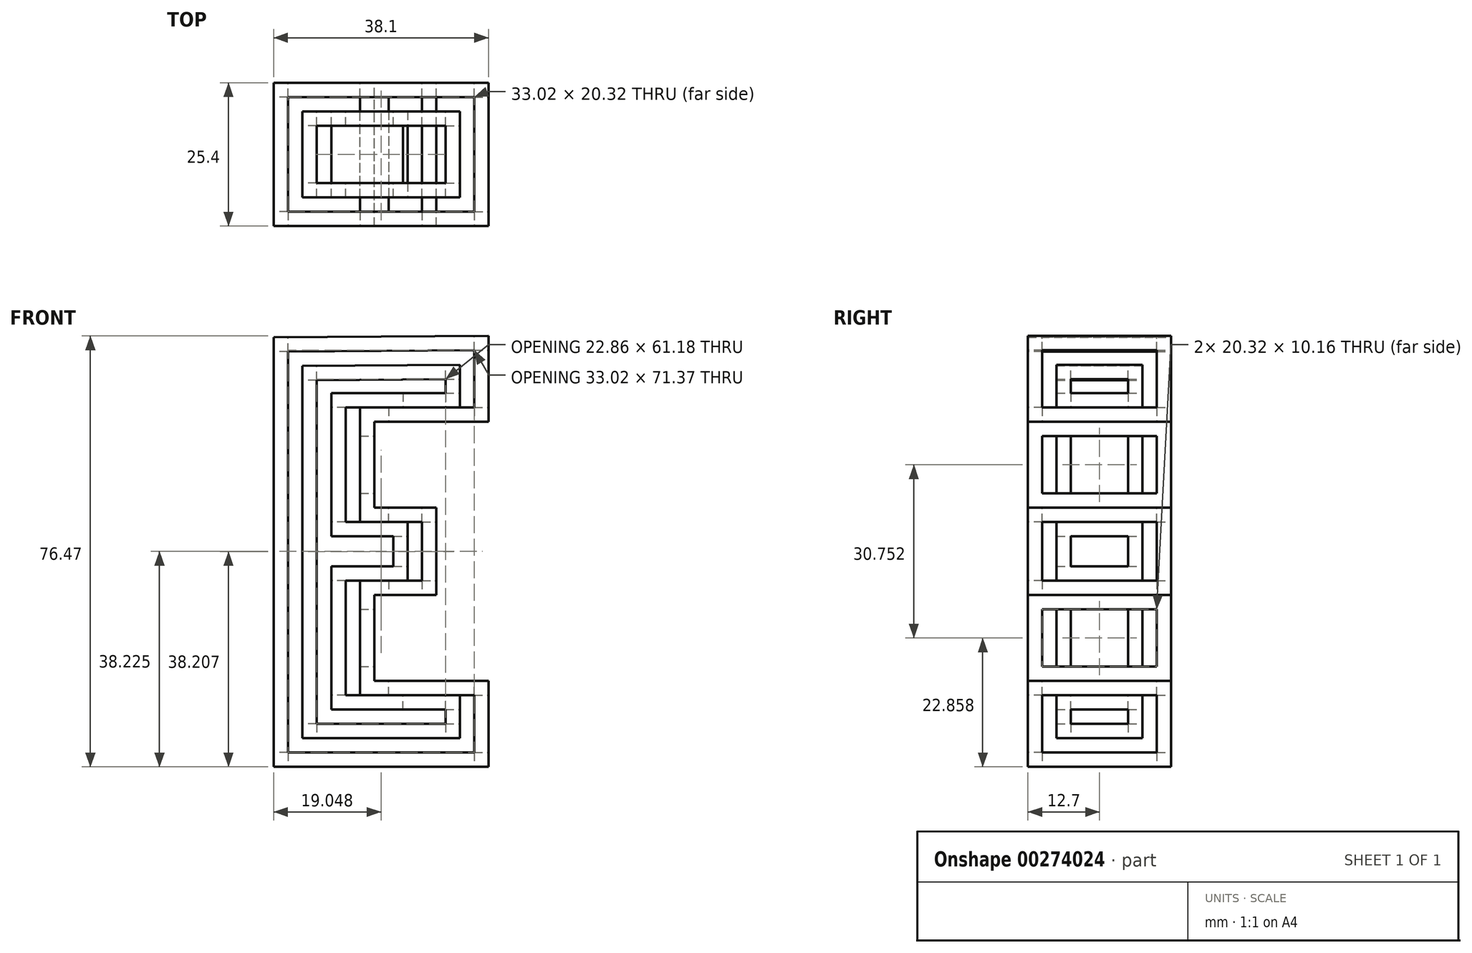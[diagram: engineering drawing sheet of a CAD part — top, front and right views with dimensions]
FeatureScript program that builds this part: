
annotation { "Feature Type Name" : "Feature", "Feature Type Description" : "" }
export const myFeature = defineFeature(function(context is Context, id is Id, definition is map)
    precondition{}
    {
        {
            var Q0;
            Q0=qCreatedBy(makeId("Front.planeOp"),FACE);
            var sketch = newSketch(context, id + "F0", { "sketchPlane" : qUnion([Q0])});
            skLineSegment(sketch, "E0", {"start": v(-49.34, 30.2) * mm, "end": v(-49.34, -46) * mm});
            skLineSegment(sketch, "E1", {"start": v(-11.24, -46) * mm, "end": v(-49.34, -46) * mm});
            skLineSegment(sketch, "E2", {"start": v(-11.24, -30.75) * mm, "end": v(-11.24, -46) * mm});
            skLineSegment(sketch, "E3", {"start": v(-31.48, -30.75) * mm, "end": v(-11.24, -30.75) * mm});
            skLineSegment(sketch, "E4", {"start": v(-31.48, -15.51) * mm, "end": v(-31.48, -30.75) * mm});
            skLineSegment(sketch, "E5", {"start": v(-20.49, -15.51) * mm, "end": v(-31.48, -15.51) * mm});
            skLineSegment(sketch, "E6", {"start": v(-20.49, 0) * mm, "end": v(-20.49, -15.51) * mm});
            skLineSegment(sketch, "E7", {"start": v(-31.48, 0) * mm, "end": v(-20.49, 0) * mm});
            skLineSegment(sketch, "E8", {"start": v(-31.48, 15.24) * mm, "end": v(-31.48, 0) * mm});
            skLineSegment(sketch, "E9", {"start": v(-31.48, 15.24) * mm, "end": v(-11.24, 15.24) * mm});
            skLineSegment(sketch, "E10", {"start": v(-11.24, 15.24) * mm, "end": v(-11.24, 30.48) * mm});
            skLineSegment(sketch, "E11", {"start": v(-11.24, 30.48) * mm, "end": v(-49.34, 30.2) * mm});
            skSolve(sketch);
        }
        {
            var Q0;
            Q0=makeQuery(id+"F0.imprint","IMPRINT",FACE,{"disambiguationData":[TD([[makeQuery(id+"F0.imprint","IMPRINT",EDGE,{"derivedFrom":sQuery(id+"F0.wireOp",EDGE,"E0")}),1.0]])]});
            extrude(context, id + "F1", {"entities" : qUnion([Q0]), "depth" : 12.7 * mm});
        }
        {
            var Q0;
            Q0=makeQuery(id+"F1.opExtrude","CAP_FACE",FACE,{"disambiguationData":[OSD([sQuery(id+"F0.wireOp",EDGE,"E0"),sQuery(id+"F0.wireOp",EDGE,"E1"),sQuery(id+"F0.wireOp",EDGE,"E2"),sQuery(id+"F0.wireOp",EDGE,"E3"),sQuery(id+"F0.wireOp",EDGE,"E4"),sQuery(id+"F0.wireOp",EDGE,"E5"),sQuery(id+"F0.wireOp",EDGE,"E6"),sQuery(id+"F0.wireOp",EDGE,"E7"),sQuery(id+"F0.wireOp",EDGE,"E8"),sQuery(id+"F0.wireOp",EDGE,"E9"),sQuery(id+"F0.wireOp",EDGE,"E10"),sQuery(id+"F0.wireOp",EDGE,"E11")])],"isStart":false});
            var sketch = newSketch(context, id + "F2", { "sketchPlane" : qUnion([Q0])});
            skLineSegment(sketch, "E12.0", {"start": v(-34.02, 17.78) * mm, "end": v(-13.78, 17.78) * mm});
            skLineSegment(sketch, "E12.1", {"start": v(-13.78, -43.45) * mm, "end": v(-13.78, -33.3) * mm});
            skLineSegment(sketch, "E12.2", {"start": v(-46.8, -43.45) * mm, "end": v(-13.78, -43.45) * mm});
            skLineSegment(sketch, "E12.3", {"start": v(-46.8, 27.69) * mm, "end": v(-46.8, -43.45) * mm});
            skLineSegment(sketch, "E12.4", {"start": v(-13.78, 27.92) * mm, "end": v(-46.8, 27.69) * mm});
            skLineSegment(sketch, "E12.5", {"start": v(-13.78, -33.3) * mm, "end": v(-34.02, -33.3) * mm});
            skLineSegment(sketch, "E12.6", {"start": v(-13.78, 17.78) * mm, "end": v(-13.78, 27.92) * mm});
            skLineSegment(sketch, "E12.7", {"start": v(-34.02, -33.3) * mm, "end": v(-34.02, -12.97) * mm});
            skLineSegment(sketch, "E12.8", {"start": v(-34.02, -12.97) * mm, "end": v(-23.03, -12.97) * mm});
            skLineSegment(sketch, "E12.9", {"start": v(-23.03, -12.97) * mm, "end": v(-23.03, -2.54) * mm});
            skLineSegment(sketch, "E12.10", {"start": v(-23.03, -2.54) * mm, "end": v(-34.02, -2.54) * mm});
            skLineSegment(sketch, "E12.11", {"start": v(-34.02, -2.54) * mm, "end": v(-34.02, 17.78) * mm});
            skSolve(sketch);
        }
        {
            var Q0;
            Q0=makeQuery(id+"F2.imprint","IMPRINT",FACE,{"disambiguationData":[TD([[makeQuery(id+"F2.imprint","IMPRINT",EDGE,{"derivedFrom":sQuery(id+"F2.wireOp",EDGE,"E12.0")}),1.0]])]});
            extrude(context, id + "F3", {"entities" : qUnion([Q0]), "operationType" : NewBodyOperationType.REMOVE, "oppositeDirection" : true, "depth" : 5.08 * mm});
        }
        {
            var Q0;
            Q0=makeQuery(id+"F1.opExtrude","SWEPT_BODY",BODY,{"disambiguationData":[OSD([sQuery(id+"F0.wireOp",EDGE,"E0"),sQuery(id+"F0.wireOp",EDGE,"E1"),sQuery(id+"F0.wireOp",EDGE,"E2"),sQuery(id+"F0.wireOp",EDGE,"E3"),sQuery(id+"F0.wireOp",EDGE,"E4"),sQuery(id+"F0.wireOp",EDGE,"E5"),sQuery(id+"F0.wireOp",EDGE,"E6"),sQuery(id+"F0.wireOp",EDGE,"E7"),sQuery(id+"F0.wireOp",EDGE,"E8"),sQuery(id+"F0.wireOp",EDGE,"E9"),sQuery(id+"F0.wireOp",EDGE,"E10"),sQuery(id+"F0.wireOp",EDGE,"E11")])]});
            var Q1;
            Q1=makeQuery(id+"F1.opExtrude","CAP_FACE",FACE,{"disambiguationData":[OSD([sQuery(id+"F0.wireOp",EDGE,"E0"),sQuery(id+"F0.wireOp",EDGE,"E1"),sQuery(id+"F0.wireOp",EDGE,"E2"),sQuery(id+"F0.wireOp",EDGE,"E3"),sQuery(id+"F0.wireOp",EDGE,"E4"),sQuery(id+"F0.wireOp",EDGE,"E5"),sQuery(id+"F0.wireOp",EDGE,"E6"),sQuery(id+"F0.wireOp",EDGE,"E7"),sQuery(id+"F0.wireOp",EDGE,"E8"),sQuery(id+"F0.wireOp",EDGE,"E9"),sQuery(id+"F0.wireOp",EDGE,"E10"),sQuery(id+"F0.wireOp",EDGE,"E11")])],"isStart":true});
            mirror(context, id + "F4", {"operationType" : NewBodyOperationType.ADD, "entities" : qUnion([Q0]), "mirrorPlane" : qUnion([Q1])});
        }
        {
            var Q0;
            {var subQ0=makeQuery(id+"F1.opExtrude","SWEPT_FACE",FACE,{"disambiguationData":[OSD([sQuery(id+"F0.wireOp",EDGE,"E11")])]});Q0=makeQuery(id+"F4.boolean.opBoolean","MERGE",FACE,{"derivedFrom":[subQ0,makeQuery(id+"F4.opPattern","COPY",FACE,{"derivedFrom":subQ0,"instanceName":"1"})]});}
            var sketch = newSketch(context, id + "F5", { "sketchPlane" : qUnion([Q0])});
            skLineSegment(sketch, "E13.0", {"start": v(-13.56, -10.16) * mm, "end": v(-13.56, 10.16) * mm});
            skLineSegment(sketch, "E13.1", {"start": v(-46.58, -10.16) * mm, "end": v(-13.56, -10.16) * mm});
            skLineSegment(sketch, "E13.2", {"start": v(-46.58, 10.16) * mm, "end": v(-46.58, -10.16) * mm});
            skLineSegment(sketch, "E13.3", {"start": v(-13.56, 10.16) * mm, "end": v(-46.58, 10.16) * mm});
            skSolve(sketch);
        }
        {
            var Q0;
            Q0=makeQuery(id+"F5.imprint","IMPRINT",FACE,{"disambiguationData":[TD([[makeQuery(id+"F5.imprint","IMPRINT",EDGE,{"derivedFrom":sQuery(id+"F5.wireOp",EDGE,"E13.0")}),1.0]])]});
            extrude(context, id + "F6", {"entities" : qUnion([Q0]), "operationType" : NewBodyOperationType.REMOVE, "oppositeDirection" : true, "depth" : 5.08 * mm});
        }
        {
            var Q0;
            {var subQ0=makeQuery(id+"F1.opExtrude","SWEPT_FACE",FACE,{"disambiguationData":[OSD([sQuery(id+"F0.wireOp",EDGE,"E0")])]});Q0=makeQuery(id+"F4.boolean.opBoolean","MERGE",FACE,{"derivedFrom":[subQ0,makeQuery(id+"F4.opPattern","COPY",FACE,{"derivedFrom":subQ0,"instanceName":"1"})]});}
            var sketch = newSketch(context, id + "F7", { "sketchPlane" : qUnion([Q0])});
            skLineSegment(sketch, "E14.0", {"start": v(10.16, 27.67) * mm, "end": v(-10.16, 27.67) * mm});
            skLineSegment(sketch, "E14.1", {"start": v(10.16, -43.45) * mm, "end": v(10.16, 27.67) * mm});
            skLineSegment(sketch, "E14.2", {"start": v(-10.16, -43.45) * mm, "end": v(10.16, -43.45) * mm});
            skLineSegment(sketch, "E14.3", {"start": v(-10.16, 27.67) * mm, "end": v(-10.16, -43.45) * mm});
            skSolve(sketch);
        }
        {
            var Q0;
            Q0=makeQuery(id+"F7.imprint","IMPRINT",FACE,{"disambiguationData":[TD([[makeQuery(id+"F7.imprint","IMPRINT",EDGE,{"derivedFrom":sQuery(id+"F7.wireOp",EDGE,"E14.0")}),1.0]])]});
            extrude(context, id + "F8", {"entities" : qUnion([Q0]), "operationType" : NewBodyOperationType.REMOVE, "oppositeDirection" : true, "depth" : 5.08 * mm});
        }
        {
            var Q0;
            {var subQ0=makeQuery(id+"F1.opExtrude","SWEPT_FACE",FACE,{"disambiguationData":[OSD([sQuery(id+"F0.wireOp",EDGE,"E1")])]});Q0=makeQuery(id+"F4.boolean.opBoolean","MERGE",FACE,{"derivedFrom":[subQ0,makeQuery(id+"F4.opPattern","COPY",FACE,{"derivedFrom":subQ0,"instanceName":"1"})]});}
            var sketch = newSketch(context, id + "F9", { "sketchPlane" : qUnion([Q0])});
            skLineSegment(sketch, "E15.0", {"start": v(-46.8, 10.16) * mm, "end": v(-46.8, -10.16) * mm});
            skLineSegment(sketch, "E15.1", {"start": v(-13.78, 10.16) * mm, "end": v(-46.8, 10.16) * mm});
            skLineSegment(sketch, "E15.2", {"start": v(-13.78, -10.16) * mm, "end": v(-13.78, 10.16) * mm});
            skLineSegment(sketch, "E15.3", {"start": v(-46.8, -10.16) * mm, "end": v(-13.78, -10.16) * mm});
            skSolve(sketch);
        }
        {
            var Q0;
            Q0=makeQuery(id+"F9.imprint","IMPRINT",FACE,{"disambiguationData":[TD([[makeQuery(id+"F9.imprint","IMPRINT",EDGE,{"derivedFrom":sQuery(id+"F9.wireOp",EDGE,"E15.0")}),1.0]])]});
            extrude(context, id + "F10", {"entities" : qUnion([Q0]), "operationType" : NewBodyOperationType.REMOVE, "oppositeDirection" : true, "depth" : 5.08 * mm});
        }
        {
            var Q0;
            {var subQ0=makeQuery(id+"F1.opExtrude","SWEPT_FACE",FACE,{"disambiguationData":[OSD([sQuery(id+"F0.wireOp",EDGE,"E10")])]});Q0=makeQuery(id+"F4.boolean.opBoolean","MERGE",FACE,{"derivedFrom":[subQ0,makeQuery(id+"F4.opPattern","COPY",FACE,{"derivedFrom":subQ0,"instanceName":"1"})]});}
            var sketch = newSketch(context, id + "F11", { "sketchPlane" : qUnion([Q0])});
            skLineSegment(sketch, "E16.0", {"start": v(-10.16, 17.78) * mm, "end": v(10.16, 17.78) * mm});
            skLineSegment(sketch, "E16.1", {"start": v(-10.16, 27.94) * mm, "end": v(-10.16, 17.78) * mm});
            skLineSegment(sketch, "E16.2", {"start": v(10.16, 27.94) * mm, "end": v(-10.16, 27.94) * mm});
            skLineSegment(sketch, "E16.3", {"start": v(10.16, 17.78) * mm, "end": v(10.16, 27.94) * mm});
            skSolve(sketch);
        }
        {
            var Q0;
            Q0=makeQuery(id+"F11.imprint","IMPRINT",FACE,{"disambiguationData":[TD([[makeQuery(id+"F11.imprint","IMPRINT",EDGE,{"derivedFrom":sQuery(id+"F11.wireOp",EDGE,"E16.0")}),1.0]])]});
            extrude(context, id + "F12", {"entities" : qUnion([Q0]), "operationType" : NewBodyOperationType.REMOVE, "oppositeDirection" : true, "depth" : 5.08 * mm});
        }
        {
            var Q0;
            {var subQ0=makeQuery(id+"F1.opExtrude","SWEPT_FACE",FACE,{"disambiguationData":[OSD([sQuery(id+"F0.wireOp",EDGE,"E6")])]});Q0=makeQuery(id+"F4.boolean.opBoolean","MERGE",FACE,{"derivedFrom":[subQ0,makeQuery(id+"F4.opPattern","COPY",FACE,{"derivedFrom":subQ0,"instanceName":"1"})]});}
            var sketch = newSketch(context, id + "F13", { "sketchPlane" : qUnion([Q0])});
            skLineSegment(sketch, "E17.0", {"start": v(-10.16, -12.97) * mm, "end": v(10.16, -12.97) * mm});
            skLineSegment(sketch, "E17.1", {"start": v(-10.16, -2.54) * mm, "end": v(-10.16, -12.97) * mm});
            skLineSegment(sketch, "E17.2", {"start": v(10.16, -2.54) * mm, "end": v(-10.16, -2.54) * mm});
            skLineSegment(sketch, "E17.3", {"start": v(10.16, -12.97) * mm, "end": v(10.16, -2.54) * mm});
            skSolve(sketch);
        }
        {
            var Q0;
            Q0=makeQuery(id+"F13.imprint","IMPRINT",FACE,{"disambiguationData":[TD([[makeQuery(id+"F13.imprint","IMPRINT",EDGE,{"derivedFrom":sQuery(id+"F13.wireOp",EDGE,"E17.0")}),1.0]])]});
            extrude(context, id + "F14", {"entities" : qUnion([Q0]), "operationType" : NewBodyOperationType.REMOVE, "oppositeDirection" : true, "depth" : 5.08 * mm});
        }
        {
            var Q0;
            {var subQ0=makeQuery(id+"F1.opExtrude","SWEPT_FACE",FACE,{"disambiguationData":[OSD([sQuery(id+"F0.wireOp",EDGE,"E2")])]});Q0=makeQuery(id+"F4.boolean.opBoolean","MERGE",FACE,{"derivedFrom":[subQ0,makeQuery(id+"F4.opPattern","COPY",FACE,{"derivedFrom":subQ0,"instanceName":"1"})]});}
            var sketch = newSketch(context, id + "F15", { "sketchPlane" : qUnion([Q0])});
            skLineSegment(sketch, "E18.0", {"start": v(-10.16, -43.45) * mm, "end": v(10.16, -43.45) * mm});
            skLineSegment(sketch, "E18.1", {"start": v(-10.16, -33.3) * mm, "end": v(-10.16, -43.45) * mm});
            skLineSegment(sketch, "E18.2", {"start": v(10.16, -33.3) * mm, "end": v(-10.16, -33.3) * mm});
            skLineSegment(sketch, "E18.3", {"start": v(10.16, -43.45) * mm, "end": v(10.16, -33.3) * mm});
            skSolve(sketch);
        }
        {
            var Q0;
            Q0=makeQuery(id+"F15.imprint","IMPRINT",FACE,{"disambiguationData":[TD([[makeQuery(id+"F15.imprint","IMPRINT",EDGE,{"derivedFrom":sQuery(id+"F15.wireOp",EDGE,"E18.0")}),1.0]])]});
            extrude(context, id + "F16", {"entities" : qUnion([Q0]), "operationType" : NewBodyOperationType.REMOVE, "oppositeDirection" : true, "depth" : 5.08 * mm});
        }
        {
            var Q0;
            {var subQ0=makeQuery(id+"F1.opExtrude","SWEPT_FACE",FACE,{"disambiguationData":[OSD([sQuery(id+"F0.wireOp",EDGE,"E8")])]});Q0=makeQuery(id+"F4.boolean.opBoolean","MERGE",FACE,{"derivedFrom":[subQ0,makeQuery(id+"F4.opPattern","COPY",FACE,{"derivedFrom":subQ0,"instanceName":"1"})]});}
            var sketch = newSketch(context, id + "F17", { "sketchPlane" : qUnion([Q0])});
            skLineSegment(sketch, "E19.0", {"start": v(-10.16, 2.54) * mm, "end": v(10.16, 2.54) * mm});
            skLineSegment(sketch, "E19.1", {"start": v(-10.16, 12.7) * mm, "end": v(-10.16, 2.54) * mm});
            skLineSegment(sketch, "E19.2", {"start": v(10.16, 12.7) * mm, "end": v(-10.16, 12.7) * mm});
            skLineSegment(sketch, "E19.3", {"start": v(10.16, 2.54) * mm, "end": v(10.16, 12.7) * mm});
            skSolve(sketch);
        }
        {
            var Q0;
            Q0=makeQuery(id+"F17.imprint","IMPRINT",FACE,{"disambiguationData":[TD([[makeQuery(id+"F17.imprint","IMPRINT",EDGE,{"derivedFrom":sQuery(id+"F17.wireOp",EDGE,"E19.0")}),1.0]])]});
            extrude(context, id + "F18", {"entities" : qUnion([Q0]), "operationType" : NewBodyOperationType.REMOVE, "oppositeDirection" : true, "depth" : 5.08 * mm});
        }
        {
            var Q0;
            {var subQ0=makeQuery(id+"F1.opExtrude","SWEPT_FACE",FACE,{"disambiguationData":[OSD([sQuery(id+"F0.wireOp",EDGE,"E4")])]});Q0=makeQuery(id+"F4.boolean.opBoolean","MERGE",FACE,{"derivedFrom":[subQ0,makeQuery(id+"F4.opPattern","COPY",FACE,{"derivedFrom":subQ0,"instanceName":"1"})]});}
            var sketch = newSketch(context, id + "F19", { "sketchPlane" : qUnion([Q0])});
            skLineSegment(sketch, "E20.0", {"start": v(-10.16, -28.21) * mm, "end": v(10.16, -28.21) * mm});
            skLineSegment(sketch, "E20.1", {"start": v(-10.16, -18.05) * mm, "end": v(-10.16, -28.21) * mm});
            skLineSegment(sketch, "E20.2", {"start": v(10.16, -18.05) * mm, "end": v(-10.16, -18.05) * mm});
            skLineSegment(sketch, "E20.3", {"start": v(10.16, -28.21) * mm, "end": v(10.16, -18.05) * mm});
            skSolve(sketch);
        }
        {
            var Q0;
            Q0=makeQuery(id+"F19.imprint","IMPRINT",FACE,{"disambiguationData":[TD([[makeQuery(id+"F19.imprint","IMPRINT",EDGE,{"derivedFrom":sQuery(id+"F19.wireOp",EDGE,"E20.0")}),1.0]])]});
            extrude(context, id + "F20", {"entities" : qUnion([Q0]), "operationType" : NewBodyOperationType.REMOVE, "oppositeDirection" : true, "depth" : 5.08 * mm});
        }
        {
            var Q0;
            {var subQ0=sQuery(id+"F2.wireOp",EDGE,"E12.10");var subQ1=sQuery(id+"F2.wireOp",EDGE,"E12.9");var subQ2=sQuery(id+"F2.wireOp",EDGE,"E12.2");var subQ3=makeQuery(id+"F3.boolean.opBoolean","COPY",FACE,{"derivedFrom":makeQuery(id+"F3.opExtrude","SWEPT_FACE",FACE,{"disambiguationData":[OSD([subQ2])]})});var subQ4=sQuery(id+"F2.wireOp",EDGE,"E12.8");var subQ5=sQuery(id+"F2.wireOp",EDGE,"E12.6");var subQ6=sQuery(id+"F2.wireOp",EDGE,"E12.5");var subQ7=sQuery(id+"F2.wireOp",EDGE,"E12.7");var subQ8=sQuery(id+"F2.wireOp",EDGE,"E12.0");var subQ9=sQuery(id+"F2.wireOp",EDGE,"E12.1");var subQ10=sQuery(id+"F2.wireOp",EDGE,"E12.11");Q0=makeQuery(id+"F8.boolean.opBoolean","SPLIT",FACE,{"disambiguationData":[TD([subQ3])],"derivedFrom":makeQuery(id+"F4.opPattern","COPY",FACE,{"derivedFrom":makeQuery(id+"F3.boolean.opBoolean","COPY",FACE,{"derivedFrom":makeQuery(id+"F3.opExtrude","CAP_FACE",FACE,{"disambiguationData":[OSD([subQ8,subQ9,subQ2,sQuery(id+"F2.wireOp",EDGE,"E12.3"),sQuery(id+"F2.wireOp",EDGE,"E12.4"),subQ6,subQ5,subQ7,subQ4,subQ1,subQ0,subQ10])],"isStart":false})}),"instanceName":"1"})});}
            var sketch = newSketch(context, id + "F21", { "sketchPlane" : qUnion([Q0])});
            skLineSegment(sketch, "E21", {"start": v(36.56, -18.05) * mm, "end": v(36.56, -12.97) * mm});
            skLineSegment(sketch, "E22", {"start": v(36.56, -12.97) * mm, "end": v(34.02, -12.97) * mm});
            skLineSegment(sketch, "E23", {"start": v(34.02, -12.97) * mm, "end": v(36.56, -12.97) * mm});
            skLineSegment(sketch, "E24", {"start": v(36.56, 2.54) * mm, "end": v(36.56, -2.54) * mm});
            skLineSegment(sketch, "E25", {"start": v(36.56, -2.54) * mm, "end": v(34.02, -2.54) * mm});
            skLineSegment(sketch, "E26", {"start": v(34.02, -2.54) * mm, "end": v(36.56, -2.54) * mm});
            skSolve(sketch);
        }
        {
            var Q0;
            Q0=makeQuery(id+"F21.imprint","IMPRINT",FACE,{"disambiguationData":[TD([[makeQuery(id+"F21.imprint","IMPRINT",EDGE,{"derivedFrom":sQuery(id+"F21.wireOp",EDGE,"E21")}),1.0]])]});
            var Q1;
            Q1=makeQuery(id+"F21.imprint","IMPRINT",FACE,{"disambiguationData":[TD([[makeQuery(id+"F21.imprint","IMPRINT",EDGE,{"derivedFrom":sQuery(id+"F21.wireOp",EDGE,"E24")}),-1.0]])]});
            extrude(context, id + "F22", {"entities" : qUnion([Q0, Q1]), "operationType" : NewBodyOperationType.REMOVE, "oppositeDirection" : true, "depth" : 25.4 * mm});
        }
        {
            var Q0;
            {var subQ0=sQuery(id+"F2.wireOp",EDGE,"E12.10");var subQ1=sQuery(id+"F2.wireOp",EDGE,"E12.9");var subQ2=sQuery(id+"F2.wireOp",EDGE,"E12.2");var subQ3=makeQuery(id+"F3.boolean.opBoolean","COPY",FACE,{"derivedFrom":makeQuery(id+"F3.opExtrude","SWEPT_FACE",FACE,{"disambiguationData":[OSD([subQ2])]})});var subQ4=sQuery(id+"F2.wireOp",EDGE,"E12.8");var subQ5=sQuery(id+"F2.wireOp",EDGE,"E12.6");var subQ6=sQuery(id+"F2.wireOp",EDGE,"E12.5");var subQ7=sQuery(id+"F2.wireOp",EDGE,"E12.7");var subQ8=sQuery(id+"F2.wireOp",EDGE,"E12.0");var subQ9=sQuery(id+"F2.wireOp",EDGE,"E12.1");var subQ10=sQuery(id+"F2.wireOp",EDGE,"E12.11");Q0=makeQuery(id+"F8.boolean.opBoolean","SPLIT",FACE,{"disambiguationData":[TD([subQ3])],"derivedFrom":makeQuery(id+"F4.opPattern","COPY",FACE,{"derivedFrom":makeQuery(id+"F3.boolean.opBoolean","COPY",FACE,{"derivedFrom":makeQuery(id+"F3.opExtrude","CAP_FACE",FACE,{"disambiguationData":[OSD([subQ8,subQ9,subQ2,sQuery(id+"F2.wireOp",EDGE,"E12.3"),sQuery(id+"F2.wireOp",EDGE,"E12.4"),subQ6,subQ5,subQ7,subQ4,subQ1,subQ0,subQ10])],"isStart":false})}),"instanceName":"1"})});}
            var sketch = newSketch(context, id + "F23", { "sketchPlane" : qUnion([Q0])});
            skLineSegment(sketch, "E27", {"start": v(36.56, -28.21) * mm, "end": v(36.56, -33.3) * mm});
            skLineSegment(sketch, "E28", {"start": v(36.56, -33.3) * mm, "end": v(34.02, -33.3) * mm});
            skLineSegment(sketch, "E29", {"start": v(34.02, -33.3) * mm, "end": v(36.56, -33.3) * mm});
            skLineSegment(sketch, "E30", {"start": v(36.56, 12.7) * mm, "end": v(36.56, 17.78) * mm});
            skLineSegment(sketch, "E31", {"start": v(36.56, 17.78) * mm, "end": v(34.02, 17.78) * mm});
            skLineSegment(sketch, "E32", {"start": v(34.02, 17.78) * mm, "end": v(36.56, 17.78) * mm});
            skSolve(sketch);
        }
        {
            var Q0;
            Q0=makeQuery(id+"F23.imprint","IMPRINT",FACE,{"disambiguationData":[TD([[makeQuery(id+"F23.imprint","IMPRINT",EDGE,{"derivedFrom":sQuery(id+"F23.wireOp",EDGE,"E27")}),-1.0]])]});
            var Q1;
            Q1=makeQuery(id+"F23.imprint","IMPRINT",FACE,{"disambiguationData":[TD([[makeQuery(id+"F23.imprint","IMPRINT",EDGE,{"derivedFrom":sQuery(id+"F23.wireOp",EDGE,"E30")}),1.0]])]});
            extrude(context, id + "F24", {"entities" : qUnion([Q0, Q1]), "operationType" : NewBodyOperationType.REMOVE, "oppositeDirection" : true, "depth" : 25.4 * mm});
        }
        {
            var Q0;
            {var subQ0=sQuery(id+"F2.wireOp",EDGE,"E12.10");var subQ1=sQuery(id+"F2.wireOp",EDGE,"E12.9");var subQ2=sQuery(id+"F2.wireOp",EDGE,"E12.2");var subQ3=makeQuery(id+"F3.boolean.opBoolean","COPY",FACE,{"derivedFrom":makeQuery(id+"F3.opExtrude","SWEPT_FACE",FACE,{"disambiguationData":[OSD([subQ2])]})});var subQ4=sQuery(id+"F2.wireOp",EDGE,"E12.8");var subQ5=sQuery(id+"F2.wireOp",EDGE,"E12.6");var subQ6=sQuery(id+"F2.wireOp",EDGE,"E12.5");var subQ7=sQuery(id+"F2.wireOp",EDGE,"E12.7");var subQ8=sQuery(id+"F2.wireOp",EDGE,"E12.0");var subQ9=sQuery(id+"F2.wireOp",EDGE,"E12.1");var subQ10=sQuery(id+"F2.wireOp",EDGE,"E12.11");Q0=makeQuery(id+"F8.boolean.opBoolean","SPLIT",FACE,{"disambiguationData":[TD([subQ3])],"derivedFrom":makeQuery(id+"F4.opPattern","COPY",FACE,{"derivedFrom":makeQuery(id+"F3.boolean.opBoolean","COPY",FACE,{"derivedFrom":makeQuery(id+"F3.opExtrude","CAP_FACE",FACE,{"disambiguationData":[OSD([subQ8,subQ9,subQ2,sQuery(id+"F2.wireOp",EDGE,"E12.3"),sQuery(id+"F2.wireOp",EDGE,"E12.4"),subQ6,subQ5,subQ7,subQ4,subQ1,subQ0,subQ10])],"isStart":false})}),"instanceName":"1"})});}
            var sketch = newSketch(context, id + "F25", { "sketchPlane" : qUnion([Q0])});
            skLineSegment(sketch, "E33.0", {"start": v(18.86, 22.8) * mm, "end": v(18.86, 20.32) * mm});
            skLineSegment(sketch, "E33.1", {"start": v(41.72, 22.64) * mm, "end": v(18.86, 22.8) * mm});
            skLineSegment(sketch, "E33.2", {"start": v(41.72, -38.37) * mm, "end": v(41.72, 22.64) * mm});
            skLineSegment(sketch, "E33.3", {"start": v(18.86, -38.37) * mm, "end": v(41.72, -38.37) * mm});
            skLineSegment(sketch, "E33.4", {"start": v(18.86, -35.83) * mm, "end": v(18.86, -38.37) * mm});
            skLineSegment(sketch, "E33.5", {"start": v(34.02, -5.08) * mm, "end": v(28.1, -5.08) * mm});
            skLineSegment(sketch, "E33.6", {"start": v(39.1, -5.08) * mm, "end": v(34.02, -5.08) * mm});
            skLineSegment(sketch, "E33.7", {"start": v(39.1, 20.32) * mm, "end": v(39.1, -5.08) * mm});
            skLineSegment(sketch, "E33.8", {"start": v(34.02, 20.32) * mm, "end": v(39.1, 20.32) * mm});
            skLineSegment(sketch, "E33.9", {"start": v(28.1, -5.08) * mm, "end": v(28.1, -10.43) * mm});
            skLineSegment(sketch, "E33.10", {"start": v(28.1, -10.43) * mm, "end": v(34.02, -10.43) * mm});
            skLineSegment(sketch, "E33.11", {"start": v(34.02, -10.43) * mm, "end": v(39.1, -10.43) * mm});
            skLineSegment(sketch, "E33.12", {"start": v(39.1, -10.43) * mm, "end": v(39.1, -35.83) * mm});
            skLineSegment(sketch, "E33.13", {"start": v(39.1, -35.83) * mm, "end": v(34.02, -35.83) * mm});
            skLineSegment(sketch, "E33.14", {"start": v(18.86, 20.32) * mm, "end": v(34.02, 20.32) * mm});
            skLineSegment(sketch, "E33.15", {"start": v(34.02, -35.83) * mm, "end": v(18.86, -35.83) * mm});
            skSolve(sketch);
        }
        {
            var Q0;
            Q0=makeQuery(id+"F25.imprint","IMPRINT",FACE,{"disambiguationData":[TD([[makeQuery(id+"F25.imprint","IMPRINT",EDGE,{"derivedFrom":sQuery(id+"F25.wireOp",EDGE,"E33.0")}),1.0]])]});
            extrude(context, id + "F26", {"entities" : qUnion([Q0]), "operationType" : NewBodyOperationType.REMOVE, "oppositeDirection" : true, "depth" : 25.4 * mm});
        }
        {
            var Q0;
            {var subQ0=makeQuery(id+"F1.opExtrude","SWEPT_FACE",FACE,{"disambiguationData":[OSD([sQuery(id+"F0.wireOp",EDGE,"E9")])]});Q0=makeQuery(id+"F4.boolean.opBoolean","MERGE",FACE,{"derivedFrom":[subQ0,makeQuery(id+"F4.opPattern","COPY",FACE,{"derivedFrom":subQ0,"instanceName":"1"})]});}
            var sketch = newSketch(context, id + "F27", { "sketchPlane" : qUnion([Q0])});
            skLineSegment(sketch, "E34.0", {"start": v(-28.94, 10.16) * mm, "end": v(-28.94, -10.16) * mm});
            skLineSegment(sketch, "E34.1", {"start": v(-13.78, 10.16) * mm, "end": v(-28.94, 10.16) * mm});
            skLineSegment(sketch, "E34.2", {"start": v(-13.78, -10.16) * mm, "end": v(-13.78, 10.16) * mm});
            skLineSegment(sketch, "E34.3", {"start": v(-28.94, -10.16) * mm, "end": v(-13.78, -10.16) * mm});
            skSolve(sketch);
        }
        {
            var Q0;
            Q0=makeQuery(id+"F27.imprint","IMPRINT",FACE,{"disambiguationData":[TD([[makeQuery(id+"F27.imprint","IMPRINT",EDGE,{"derivedFrom":sQuery(id+"F27.wireOp",EDGE,"E34.0")}),1.0]])]});
            extrude(context, id + "F28", {"entities" : qUnion([Q0]), "operationType" : NewBodyOperationType.REMOVE, "oppositeDirection" : true, "depth" : 2.54 * mm});
        }
        {
            var Q0;
            {var subQ0=makeQuery(id+"F1.opExtrude","SWEPT_FACE",FACE,{"disambiguationData":[OSD([sQuery(id+"F0.wireOp",EDGE,"E3")])]});Q0=makeQuery(id+"F4.boolean.opBoolean","MERGE",FACE,{"derivedFrom":[subQ0,makeQuery(id+"F4.opPattern","COPY",FACE,{"derivedFrom":subQ0,"instanceName":"1"})]});}
            var sketch = newSketch(context, id + "F29", { "sketchPlane" : qUnion([Q0])});
            skLineSegment(sketch, "E35.0", {"start": v(-13.78, -10.16) * mm, "end": v(-13.78, 10.16) * mm});
            skLineSegment(sketch, "E35.1", {"start": v(-28.94, -10.16) * mm, "end": v(-13.78, -10.16) * mm});
            skLineSegment(sketch, "E35.2", {"start": v(-28.94, 10.16) * mm, "end": v(-28.94, -10.16) * mm});
            skLineSegment(sketch, "E35.3", {"start": v(-13.78, 10.16) * mm, "end": v(-28.94, 10.16) * mm});
            skSolve(sketch);
        }
        {
            var Q0;
            Q0=makeQuery(id+"F29.imprint","IMPRINT",FACE,{"disambiguationData":[TD([[makeQuery(id+"F29.imprint","IMPRINT",EDGE,{"derivedFrom":sQuery(id+"F29.wireOp",EDGE,"E35.0")}),1.0]])]});
            extrude(context, id + "F30", {"entities" : qUnion([Q0]), "operationType" : NewBodyOperationType.REMOVE, "oppositeDirection" : true, "depth" : 2.54 * mm});
        }
        {
            var Q0;
            {var subQ0=makeQuery(id+"F1.opExtrude","SWEPT_FACE",FACE,{"disambiguationData":[OSD([sQuery(id+"F0.wireOp",EDGE,"E5")])]});Q0=makeQuery(id+"F4.boolean.opBoolean","MERGE",FACE,{"derivedFrom":[subQ0,makeQuery(id+"F4.opPattern","COPY",FACE,{"derivedFrom":subQ0,"instanceName":"1"})]});}
            var sketch = newSketch(context, id + "F31", { "sketchPlane" : qUnion([Q0])});
            skLineSegment(sketch, "E36.0", {"start": v(-28.94, 10.16) * mm, "end": v(-28.94, -10.16) * mm});
            skLineSegment(sketch, "E36.1", {"start": v(-23.03, 10.16) * mm, "end": v(-28.94, 10.16) * mm});
            skLineSegment(sketch, "E36.2", {"start": v(-23.03, -10.16) * mm, "end": v(-23.03, 10.16) * mm});
            skLineSegment(sketch, "E36.3", {"start": v(-28.94, -10.16) * mm, "end": v(-23.03, -10.16) * mm});
            skSolve(sketch);
        }
        {
            var Q0;
            Q0=makeQuery(id+"F31.imprint","IMPRINT",FACE,{"disambiguationData":[TD([[makeQuery(id+"F31.imprint","IMPRINT",EDGE,{"derivedFrom":sQuery(id+"F31.wireOp",EDGE,"E36.0")}),1.0]])]});
            extrude(context, id + "F32", {"entities" : qUnion([Q0]), "operationType" : NewBodyOperationType.REMOVE, "oppositeDirection" : true, "depth" : 2.54 * mm});
        }
        {
            var Q0;
            {var subQ0=makeQuery(id+"F1.opExtrude","SWEPT_FACE",FACE,{"disambiguationData":[OSD([sQuery(id+"F0.wireOp",EDGE,"E7")])]});Q0=makeQuery(id+"F4.boolean.opBoolean","MERGE",FACE,{"derivedFrom":[subQ0,makeQuery(id+"F4.opPattern","COPY",FACE,{"derivedFrom":subQ0,"instanceName":"1"})]});}
            var sketch = newSketch(context, id + "F33", { "sketchPlane" : qUnion([Q0])});
            skLineSegment(sketch, "E37.0", {"start": v(-23.03, -10.16) * mm, "end": v(-23.03, 10.16) * mm});
            skLineSegment(sketch, "E37.1", {"start": v(-28.94, -10.16) * mm, "end": v(-23.03, -10.16) * mm});
            skLineSegment(sketch, "E37.2", {"start": v(-28.94, 10.16) * mm, "end": v(-28.94, -10.16) * mm});
            skLineSegment(sketch, "E37.3", {"start": v(-23.03, 10.16) * mm, "end": v(-28.94, 10.16) * mm});
            skSolve(sketch);
        }
        {
            var Q0;
            Q0=makeQuery(id+"F33.imprint","IMPRINT",FACE,{"disambiguationData":[TD([[makeQuery(id+"F33.imprint","IMPRINT",EDGE,{"derivedFrom":sQuery(id+"F33.wireOp",EDGE,"E37.0")}),1.0]])]});
            extrude(context, id + "F34", {"entities" : qUnion([Q0]), "operationType" : NewBodyOperationType.REMOVE, "oppositeDirection" : true, "depth" : 2.54 * mm});
        }
        {
            var Q0;
            Q0=makeQuery(id+"F10.boolean.opBoolean","COPY",FACE,{"derivedFrom":makeQuery(id+"F10.opExtrude","CAP_FACE",FACE,{"disambiguationData":[OSD([sQuery(id+"F9.wireOp",EDGE,"E15.0"),sQuery(id+"F9.wireOp",EDGE,"E15.1"),sQuery(id+"F9.wireOp",EDGE,"E15.2"),sQuery(id+"F9.wireOp",EDGE,"E15.3")])],"isStart":false})});
            var sketch = newSketch(context, id + "F35", { "sketchPlane" : qUnion([Q0])});
            skLineSegment(sketch, "E38.0", {"start": v(-41.72, -5.08) * mm, "end": v(-18.86, -5.08) * mm});
            skLineSegment(sketch, "E38.1", {"start": v(-41.72, 5.08) * mm, "end": v(-41.72, -5.08) * mm});
            skLineSegment(sketch, "E38.2", {"start": v(-18.86, 5.08) * mm, "end": v(-41.72, 5.08) * mm});
            skLineSegment(sketch, "E38.3", {"start": v(-18.86, -5.08) * mm, "end": v(-18.86, 5.08) * mm});
            skSolve(sketch);
        }
        {
            var Q0;
            Q0=makeQuery(id+"F35.imprint","IMPRINT",FACE,{"disambiguationData":[TD([[makeQuery(id+"F35.imprint","IMPRINT",EDGE,{"derivedFrom":sQuery(id+"F35.wireOp",EDGE,"E38.0")}),1.0]])]});
            extrude(context, id + "F36", {"entities" : qUnion([Q0]), "operationType" : NewBodyOperationType.REMOVE, "oppositeDirection" : true, "depth" : 2.54 * mm});
        }
        {
            var Q0;
            Q0=makeQuery(id+"F6.boolean.opBoolean","COPY",FACE,{"derivedFrom":makeQuery(id+"F6.opExtrude","CAP_FACE",FACE,{"disambiguationData":[OSD([sQuery(id+"F5.wireOp",EDGE,"E13.0"),sQuery(id+"F5.wireOp",EDGE,"E13.1"),sQuery(id+"F5.wireOp",EDGE,"E13.2"),sQuery(id+"F5.wireOp",EDGE,"E13.3")])],"isStart":false})});
            var sketch = newSketch(context, id + "F37", { "sketchPlane" : qUnion([Q0])});
            skLineSegment(sketch, "E39.0", {"start": v(-41.54, -5.08) * mm, "end": v(-18.68, -5.08) * mm});
            skLineSegment(sketch, "E39.1", {"start": v(-41.54, 5.08) * mm, "end": v(-41.54, -5.08) * mm});
            skLineSegment(sketch, "E39.2", {"start": v(-18.68, 5.08) * mm, "end": v(-41.54, 5.08) * mm});
            skLineSegment(sketch, "E39.3", {"start": v(-18.68, -5.08) * mm, "end": v(-18.68, 5.08) * mm});
            skSolve(sketch);
        }
        {
            var Q0;
            Q0=makeQuery(id+"F37.imprint","IMPRINT",FACE,{"disambiguationData":[TD([[makeQuery(id+"F37.imprint","IMPRINT",EDGE,{"derivedFrom":sQuery(id+"F37.wireOp",EDGE,"E39.0")}),1.0]])]});
            extrude(context, id + "F38", {"entities" : qUnion([Q0]), "operationType" : NewBodyOperationType.REMOVE, "oppositeDirection" : true, "depth" : 2.54 * mm});
        }
        {
            var Q0;
            Q0=makeQuery(id+"F28.boolean.opBoolean","COPY",FACE,{"derivedFrom":makeQuery(id+"F28.opExtrude","CAP_FACE",FACE,{"disambiguationData":[OSD([sQuery(id+"F27.wireOp",EDGE,"E34.0"),sQuery(id+"F27.wireOp",EDGE,"E34.1"),sQuery(id+"F27.wireOp",EDGE,"E34.2"),sQuery(id+"F27.wireOp",EDGE,"E34.3")])],"isStart":false})});
            var sketch = newSketch(context, id + "F39", { "sketchPlane" : qUnion([Q0])});
            skLineSegment(sketch, "E40.0", {"start": v(-26.4, -5.08) * mm, "end": v(-18.86, -5.08) * mm});
            skLineSegment(sketch, "E40.1", {"start": v(-26.4, 5.08) * mm, "end": v(-26.4, -5.08) * mm});
            skLineSegment(sketch, "E40.2", {"start": v(-18.86, 5.08) * mm, "end": v(-26.4, 5.08) * mm});
            skLineSegment(sketch, "E40.3", {"start": v(-18.86, -5.08) * mm, "end": v(-18.86, 5.08) * mm});
            skSolve(sketch);
        }
        {
            var Q0;
            Q0=makeQuery(id+"F39.imprint","IMPRINT",FACE,{"disambiguationData":[TD([[makeQuery(id+"F39.imprint","IMPRINT",EDGE,{"derivedFrom":sQuery(id+"F39.wireOp",EDGE,"E40.0")}),1.0]])]});
            extrude(context, id + "F40", {"entities" : qUnion([Q0]), "operationType" : NewBodyOperationType.REMOVE, "oppositeDirection" : true, "depth" : 2.54 * mm});
        }
        {
            var Q0;
            Q0=makeQuery(id+"F30.boolean.opBoolean","COPY",FACE,{"derivedFrom":makeQuery(id+"F30.opExtrude","CAP_FACE",FACE,{"disambiguationData":[OSD([sQuery(id+"F29.wireOp",EDGE,"E35.0"),sQuery(id+"F29.wireOp",EDGE,"E35.1"),sQuery(id+"F29.wireOp",EDGE,"E35.2"),sQuery(id+"F29.wireOp",EDGE,"E35.3")])],"isStart":false})});
            var sketch = newSketch(context, id + "F41", { "sketchPlane" : qUnion([Q0])});
            skLineSegment(sketch, "E41.0", {"start": v(-18.86, -5.08) * mm, "end": v(-18.86, 5.08) * mm});
            skLineSegment(sketch, "E41.1", {"start": v(-26.4, -5.08) * mm, "end": v(-18.86, -5.08) * mm});
            skLineSegment(sketch, "E41.2", {"start": v(-26.4, 5.08) * mm, "end": v(-26.4, -5.08) * mm});
            skLineSegment(sketch, "E41.3", {"start": v(-18.86, 5.08) * mm, "end": v(-26.4, 5.08) * mm});
            skSolve(sketch);
        }
        {
            var Q0;
            Q0=makeQuery(id+"F41.imprint","IMPRINT",FACE,{"disambiguationData":[TD([[makeQuery(id+"F41.imprint","IMPRINT",EDGE,{"derivedFrom":sQuery(id+"F41.wireOp",EDGE,"E41.0")}),1.0]])]});
            extrude(context, id + "F42", {"entities" : qUnion([Q0]), "operationType" : NewBodyOperationType.REMOVE, "oppositeDirection" : true, "depth" : 2.54 * mm});
        }
        {
            var Q0;
            Q0=makeQuery(id+"F14.boolean.opBoolean","COPY",FACE,{"derivedFrom":makeQuery(id+"F14.opExtrude","CAP_FACE",FACE,{"disambiguationData":[OSD([sQuery(id+"F13.wireOp",EDGE,"E17.0"),sQuery(id+"F13.wireOp",EDGE,"E17.1"),sQuery(id+"F13.wireOp",EDGE,"E17.2"),sQuery(id+"F13.wireOp",EDGE,"E17.3")])],"isStart":false})});
            var sketch = newSketch(context, id + "F43", { "sketchPlane" : qUnion([Q0])});
            skLineSegment(sketch, "E42.0", {"start": v(-5.08, -10.43) * mm, "end": v(5.08, -10.43) * mm});
            skLineSegment(sketch, "E42.1", {"start": v(-5.08, -5.08) * mm, "end": v(-5.08, -10.43) * mm});
            skLineSegment(sketch, "E42.2", {"start": v(5.08, -5.08) * mm, "end": v(-5.08, -5.08) * mm});
            skLineSegment(sketch, "E42.3", {"start": v(5.08, -10.43) * mm, "end": v(5.08, -5.08) * mm});
            skSolve(sketch);
        }
        {
            var Q0;
            Q0=makeQuery(id+"F43.imprint","IMPRINT",FACE,{"disambiguationData":[TD([[makeQuery(id+"F43.imprint","IMPRINT",EDGE,{"derivedFrom":sQuery(id+"F43.wireOp",EDGE,"E42.0")}),1.0]])]});
            extrude(context, id + "F44", {"entities" : qUnion([Q0]), "operationType" : NewBodyOperationType.REMOVE, "oppositeDirection" : true, "depth" : 2.54 * mm});
        }
        {
            var Q0;
            Q0=makeQuery(id+"F16.boolean.opBoolean","COPY",FACE,{"derivedFrom":makeQuery(id+"F16.opExtrude","CAP_FACE",FACE,{"disambiguationData":[OSD([sQuery(id+"F15.wireOp",EDGE,"E18.0"),sQuery(id+"F15.wireOp",EDGE,"E18.1"),sQuery(id+"F15.wireOp",EDGE,"E18.2"),sQuery(id+"F15.wireOp",EDGE,"E18.3")])],"isStart":false})});
            var sketch = newSketch(context, id + "F45", { "sketchPlane" : qUnion([Q0])});
            skLineSegment(sketch, "E43.0", {"start": v(-5.08, -38.37) * mm, "end": v(5.08, -38.37) * mm});
            skLineSegment(sketch, "E43.1", {"start": v(-5.08, -35.83) * mm, "end": v(-5.08, -38.37) * mm});
            skLineSegment(sketch, "E43.2", {"start": v(5.08, -35.83) * mm, "end": v(-5.08, -35.83) * mm});
            skLineSegment(sketch, "E43.3", {"start": v(5.08, -38.37) * mm, "end": v(5.08, -35.83) * mm});
            skSolve(sketch);
        }
        {
            var Q0;
            Q0=makeQuery(id+"F45.imprint","IMPRINT",FACE,{"disambiguationData":[TD([[makeQuery(id+"F45.imprint","IMPRINT",EDGE,{"derivedFrom":sQuery(id+"F45.wireOp",EDGE,"E43.0")}),1.0]])]});
            extrude(context, id + "F46", {"entities" : qUnion([Q0]), "operationType" : NewBodyOperationType.REMOVE, "oppositeDirection" : true, "depth" : 2.54 * mm});
        }
        {
            var Q0;
            Q0=makeQuery(id+"F12.boolean.opBoolean","COPY",FACE,{"derivedFrom":makeQuery(id+"F12.opExtrude","CAP_FACE",FACE,{"disambiguationData":[OSD([sQuery(id+"F11.wireOp",EDGE,"E16.0"),sQuery(id+"F11.wireOp",EDGE,"E16.1"),sQuery(id+"F11.wireOp",EDGE,"E16.2"),sQuery(id+"F11.wireOp",EDGE,"E16.3")])],"isStart":false})});
            var sketch = newSketch(context, id + "F47", { "sketchPlane" : qUnion([Q0])});
            skLineSegment(sketch, "E44.0", {"start": v(-5.08, 20.32) * mm, "end": v(5.08, 20.32) * mm});
            skLineSegment(sketch, "E44.1", {"start": v(-5.08, 22.82) * mm, "end": v(-5.08, 20.32) * mm});
            skLineSegment(sketch, "E44.2", {"start": v(5.08, 22.82) * mm, "end": v(-5.08, 22.82) * mm});
            skLineSegment(sketch, "E44.3", {"start": v(5.08, 20.32) * mm, "end": v(5.08, 22.82) * mm});
            skSolve(sketch);
        }
        {
            var Q0;
            Q0=makeQuery(id+"F47.imprint","IMPRINT",FACE,{"disambiguationData":[TD([[makeQuery(id+"F47.imprint","IMPRINT",EDGE,{"derivedFrom":sQuery(id+"F47.wireOp",EDGE,"E44.0")}),1.0]])]});
            extrude(context, id + "F48", {"entities" : qUnion([Q0]), "operationType" : NewBodyOperationType.REMOVE, "oppositeDirection" : true, "depth" : 2.54 * mm});
        }
        {
            var Q0;
            Q0=makeQuery(id+"F8.boolean.opBoolean","COPY",FACE,{"derivedFrom":makeQuery(id+"F8.opExtrude","CAP_FACE",FACE,{"disambiguationData":[OSD([sQuery(id+"F7.wireOp",EDGE,"E14.0"),sQuery(id+"F7.wireOp",EDGE,"E14.1"),sQuery(id+"F7.wireOp",EDGE,"E14.2"),sQuery(id+"F7.wireOp",EDGE,"E14.3")])],"isStart":false})});
            var sketch = newSketch(context, id + "F49", { "sketchPlane" : qUnion([Q0])});
            skLineSegment(sketch, "E45.0", {"start": v(-5.08, 22.62) * mm, "end": v(-5.08, -38.37) * mm});
            skLineSegment(sketch, "E45.1", {"start": v(5.08, 22.62) * mm, "end": v(-5.08, 22.62) * mm});
            skLineSegment(sketch, "E45.2", {"start": v(5.08, -38.37) * mm, "end": v(5.08, 22.62) * mm});
            skLineSegment(sketch, "E45.3", {"start": v(-5.08, -38.37) * mm, "end": v(5.08, -38.37) * mm});
            skSolve(sketch);
        }
        {
            var Q0;
            Q0=makeQuery(id+"F49.imprint","IMPRINT",FACE,{"disambiguationData":[TD([[makeQuery(id+"F49.imprint","IMPRINT",EDGE,{"derivedFrom":sQuery(id+"F49.wireOp",EDGE,"E45.0")}),1.0]])]});
            extrude(context, id + "F50", {"entities" : qUnion([Q0]), "operationType" : NewBodyOperationType.REMOVE, "oppositeDirection" : true, "depth" : 2.54 * mm});
        }
        {
            var Q0;
            Q0=makeQuery(id+"F26.boolean.opBoolean","COPY",FACE,{"derivedFrom":makeQuery(id+"F26.opExtrude","SWEPT_FACE",FACE,{"disambiguationData":[OSD([sQuery(id+"F25.wireOp",EDGE,"E33.12")])]})});
            var sketch = newSketch(context, id + "F51", { "sketchPlane" : qUnion([Q0])});
            skLineSegment(sketch, "E46.0", {"start": v(5.08, -33.3) * mm, "end": v(5.08, -12.97) * mm});
            skLineSegment(sketch, "E46.1", {"start": v(-5.08, -33.3) * mm, "end": v(5.08, -33.3) * mm});
            skLineSegment(sketch, "E46.2", {"start": v(-5.08, -12.97) * mm, "end": v(-5.08, -33.3) * mm});
            skLineSegment(sketch, "E46.3", {"start": v(5.08, -12.97) * mm, "end": v(-5.08, -12.97) * mm});
            skSolve(sketch);
        }
        {
            var Q0;
            Q0=makeQuery(id+"F51.imprint","IMPRINT",FACE,{"disambiguationData":[TD([[makeQuery(id+"F51.imprint","IMPRINT",EDGE,{"derivedFrom":sQuery(id+"F51.wireOp",EDGE,"E46.0")}),1.0]])]});
            extrude(context, id + "F52", {"entities" : qUnion([Q0]), "operationType" : NewBodyOperationType.REMOVE, "oppositeDirection" : true, "depth" : 2.54 * mm});
        }
        {
            var Q0;
            Q0=makeQuery(id+"F26.boolean.opBoolean","COPY",FACE,{"derivedFrom":makeQuery(id+"F26.opExtrude","SWEPT_FACE",FACE,{"disambiguationData":[OSD([sQuery(id+"F25.wireOp",EDGE,"E33.7")])]})});
            var sketch = newSketch(context, id + "F53", { "sketchPlane" : qUnion([Q0])});
            skLineSegment(sketch, "E47.0", {"start": v(5.08, -2.54) * mm, "end": v(5.08, 17.78) * mm});
            skLineSegment(sketch, "E47.1", {"start": v(-5.08, -2.54) * mm, "end": v(5.08, -2.54) * mm});
            skLineSegment(sketch, "E47.2", {"start": v(-5.08, 17.78) * mm, "end": v(-5.08, -2.54) * mm});
            skLineSegment(sketch, "E47.3", {"start": v(5.08, 17.78) * mm, "end": v(-5.08, 17.78) * mm});
            skSolve(sketch);
        }
        {
            var Q0;
            Q0=makeQuery(id+"F53.imprint","IMPRINT",FACE,{"disambiguationData":[TD([[makeQuery(id+"F53.imprint","IMPRINT",EDGE,{"derivedFrom":sQuery(id+"F53.wireOp",EDGE,"E47.0")}),1.0]])]});
            extrude(context, id + "F54", {"entities" : qUnion([Q0]), "operationType" : NewBodyOperationType.REMOVE, "oppositeDirection" : true, "depth" : 2.54 * mm});
        }
    });
